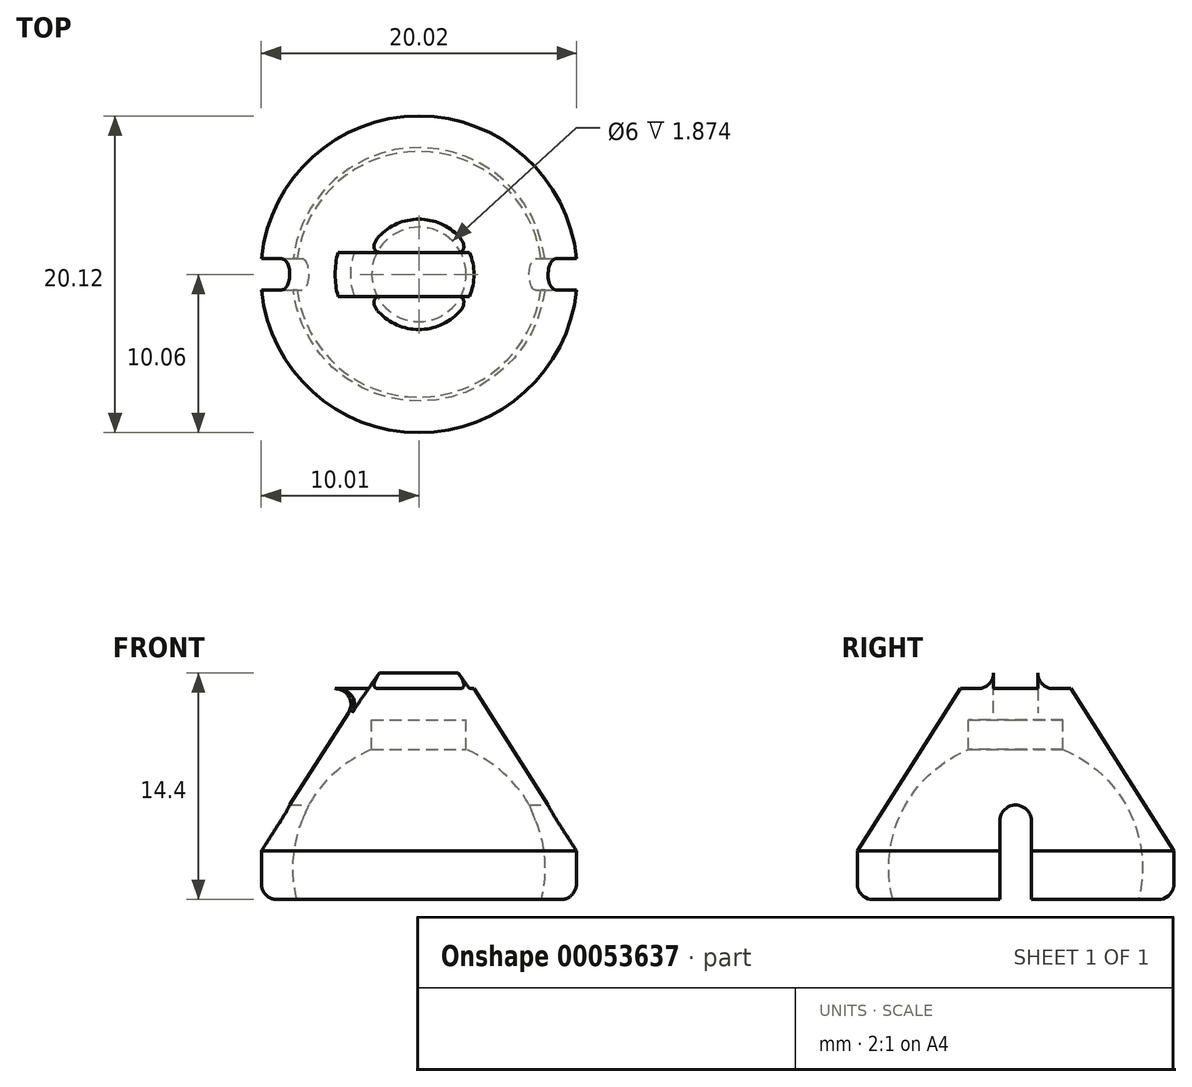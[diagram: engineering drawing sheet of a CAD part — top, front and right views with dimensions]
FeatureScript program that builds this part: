
annotation { "Feature Type Name" : "Feature", "Feature Type Description" : "" }
export const myFeature = defineFeature(function(context is Context, id is Id, definition is map)
    precondition{}
    {
        {
            var Q0;
            Q0=qCreatedBy(makeId("Front.planeOp"),FACE);
            var sketch = newSketch(context, id + "F0", { "sketchPlane" : qUnion([Q0])});
            skArc(sketch, "E0", {"start": v(0, 4.09) * mm, "mid": v(0.48, 4.1) * mm, "end": v(0.97, 4.15) * mm});
            skLineSegment(sketch, "E1", {"start": v(3.5, 7.49) * mm, "end": v(10.06, -2.83) * mm});
            skLineSegment(sketch, "E2", {"start": v(10.06, -2.83) * mm, "end": v(10.06, -5.91) * mm});
            skLineSegment(sketch, "E3", {"start": v(10.06, -5.91) * mm, "end": v(7.8, -5.91) * mm});
            skArc(sketch, "E4", {"start": v(7.8, -5.91) * mm, "mid": v(6.65, 0.66) * mm, "end": v(0.97, 4.15) * mm});
            skPoint(sketch, "E5.orphan", {"position": v(0, -5.91) * mm});
            skLineSegment(sketch, "E6", {"start": v(0, 4.09) * mm, "end": v(0, -5.91) * mm, "construction": true});
            skLineSegment(sketch, "E7", {"start": v(0, 4.09) * mm, "end": v(0, 7.49) * mm});
            skLineSegment(sketch, "E8", {"start": v(0, 7.49) * mm, "end": v(0, 9.49) * mm});
            skLineSegment(sketch, "E9", {"start": v(0, 9.49) * mm, "end": v(3.5, 9.49) * mm});
            skLineSegment(sketch, "E10", {"start": v(3.5, 9.49) * mm, "end": v(3.5, 7.49) * mm});
            skSolve(sketch);
        }
        {
            var Q0;
            Q0=qSketchRegion(id+"F0",true);
            var Q1;
            Q1=sQuery(id+"F0.wireOp",EDGE,"E6");
            revolve(context, id + "F1", {"entities" : qUnion([Q0]), "axis" : qUnion([Q1]), "revolveType" : RevolveType.FULL});
        }
        {
            var Q0;
            Q0=qCreatedBy(makeId("Top.planeOp"),FACE);
            var sketch = newSketch(context, id + "F2", { "sketchPlane" : qUnion([Q0])});
            skCircle(sketch, "E11", {"center": v(0, 0) * mm, "radius": 3 * mm});
            skSolve(sketch);
        }
        {
            var Q0;
            Q0=qSketchRegion(id+"F2",true);
            extrude(context, id + "F3", {"entities" : qUnion([Q0]), "operationType" : NewBodyOperationType.REMOVE, "endBound" : BoundingType.SYMMETRIC, "oppositeDirection" : true, "depth" : 50 * mm});
        }
        {
            var Q0;
            Q0=qCreatedBy(makeId("Right.planeOp"),FACE);
            var sketch = newSketch(context, id + "F4", { "sketchPlane" : qUnion([Q0])});
            skLineSegment(sketch, "E12.bottom", {"start": v(1, -5.91) * mm, "end": v(-1, -5.91) * mm});
            skLineSegment(sketch, "E12.left", {"start": v(1, -5.91) * mm, "end": v(1, -0.91) * mm});
            skLineSegment(sketch, "E12.right", {"start": v(-1, -5.91) * mm, "end": v(-1, -0.91) * mm});
            skArc(sketch, "E13", {"start": v(1, -0.91) * mm, "mid": v(0, 0.09) * mm, "end": v(-1, -0.91) * mm});
            skSolve(sketch);
        }
        {
            var Q0;
            Q0=qSketchRegion(id+"F4",true);
            extrude(context, id + "F5", {"entities" : qUnion([Q0]), "operationType" : NewBodyOperationType.REMOVE, "endBound" : BoundingType.SYMMETRIC, "oppositeDirection" : true, "depth" : 25 * mm});
        }
        {
            var Q0;
            Q0=makeQuery(id+"F1.opRevolve","SWEPT_EDGE",EDGE,{"disambiguationData":[OSD([sQuery(id+"F0.wireOp",EDGE,"E9"),sQuery(id+"F0.wireOp",EDGE,"E10")])]});
            fillet(context, id + "F6", {"entities" : qUnion([Q0]), "radius" : 1 * mm, "tangentPropagation" : true, "allowEdgeOverflow" : false});
        }
        {
            var Q0;
            {var subQ0=sQuery(id+"F0.wireOp",EDGE,"E2");var subQ1=sQuery(id+"F0.wireOp",EDGE,"E3");Q0=makeQuery(id+"F5.boolean.opBoolean","SPLIT",EDGE,{"disambiguationData":[TD([makeQuery(id+"F5.opExtrude","SWEPT_FACE",FACE,{"disambiguationData":[OSD([sQuery(id+"F4.wireOp",EDGE,"E12.right")])]})])],"derivedFrom":makeQuery(id+"F1.opRevolve","SWEPT_EDGE",EDGE,{"disambiguationData":[OSD([subQ0,subQ1])]})});}
            var Q1;
            {var subQ0=sQuery(id+"F0.wireOp",EDGE,"E2");var subQ1=sQuery(id+"F0.wireOp",EDGE,"E3");Q1=makeQuery(id+"F5.boolean.opBoolean","SPLIT",EDGE,{"disambiguationData":[TD([makeQuery(id+"F5.opExtrude","SWEPT_FACE",FACE,{"disambiguationData":[OSD([sQuery(id+"F4.wireOp",EDGE,"E12.left")])]})])],"derivedFrom":makeQuery(id+"F1.opRevolve","SWEPT_EDGE",EDGE,{"disambiguationData":[OSD([subQ0,subQ1])]})});}
            fillet(context, id + "F7", {"entities" : qUnion([Q0, Q1]), "radius" : 1 * mm, "tangentPropagation" : true, "allowEdgeOverflow" : false});
        }
        {
            var Q0;
            Q0=qCreatedBy(makeId("Front.planeOp"),FACE);
            var sketch = newSketch(context, id + "F8", { "sketchPlane" : qUnion([Q0])});
            skLineSegment(sketch, "E14.bottom", {"start": v(-13.5, 17.49) * mm, "end": v(13.5, 17.49) * mm});
            skLineSegment(sketch, "E14.top", {"start": v(-13.5, 7.49) * mm, "end": v(13.5, 7.49) * mm});
            skLineSegment(sketch, "E14.left", {"start": v(-13.5, 17.49) * mm, "end": v(-13.5, 7.49) * mm});
            skLineSegment(sketch, "E14.right", {"start": v(13.5, 17.49) * mm, "end": v(13.5, 7.49) * mm});
            skSolve(sketch);
        }
        {
            var Q0;
            Q0 = qSketchRegion(id + "F8", true);
            extrude(context, id + "F9", {"entities" : qUnion([Q0]), "operationType" : NewBodyOperationType.ADD, "endBound" : BoundingType.SYMMETRIC, "depth" : 7 * mm, "offsetDistance" : 25 * mm});
        }
        {
            var Q0;
            Q0=makeQuery(id+"F9.opExtrude","SWEPT_FACE",FACE,{"disambiguationData":[OSD([sQuery(id+"F8.wireOp",EDGE,"E14.bottom")])]});
            var sketch = newSketch(context, id + "F10", { "sketchPlane" : qUnion([Q0])});
            skLineSegment(sketch, "E15.bottom", {"start": v(-12.75, 2.5) * mm, "end": v(-11.5, 2.5) * mm});
            skLineSegment(sketch, "E15.top", {"start": v(-12.75, 1.4) * mm, "end": v(12.75, 1.4) * mm});
            skLineSegment(sketch, "E15.left", {"start": v(-12.75, 2.5) * mm, "end": v(-12.75, 1.4) * mm});
            skLineSegment(sketch, "E15.right", {"start": v(12.75, 2.5) * mm, "end": v(12.75, 1.4) * mm});
            skLineSegment(sketch, "E16", {"start": v(-11.5, 2.5) * mm, "end": v(-11.5, 3.5) * mm});
            skLineSegment(sketch, "E17", {"start": v(-11.5, 3.5) * mm, "end": v(11.5, 3.5) * mm});
            skLineSegment(sketch, "E18", {"start": v(11.5, 3.5) * mm, "end": v(11.5, 2.5) * mm});
            skLineSegment(sketch, "E19.trimOffspring", {"start": v(11.5, 2.5) * mm, "end": v(12.75, 2.5) * mm});
            skLineSegment(sketch, "E20.MirrorCS", {"start": v(-11.5, -3.5) * mm, "end": v(11.5, -3.5) * mm});
            skLineSegment(sketch, "E21.MirrorCS", {"start": v(-12.75, -1.4) * mm, "end": v(12.75, -1.4) * mm});
            skLineSegment(sketch, "E22.MirrorCS", {"start": v(12.75, -2.5) * mm, "end": v(12.75, -1.4) * mm});
            skLineSegment(sketch, "E23.MirrorCS", {"start": v(11.5, -2.5) * mm, "end": v(12.75, -2.5) * mm});
            skLineSegment(sketch, "E24.MirrorCS", {"start": v(11.5, -3.5) * mm, "end": v(11.5, -2.5) * mm});
            skLineSegment(sketch, "E25.MirrorCS", {"start": v(-11.5, -2.5) * mm, "end": v(-11.5, -3.5) * mm});
            skLineSegment(sketch, "E26.MirrorCS", {"start": v(-12.75, -2.5) * mm, "end": v(-11.5, -2.5) * mm});
            skLineSegment(sketch, "E27.MirrorCS", {"start": v(-12.75, -2.5) * mm, "end": v(-12.75, -1.4) * mm});
            skSolve(sketch);
        }
        {
            var Q0;
            Q0 = qSketchRegion(id + "F10", true);
            var Q1;
            {var subQ0=sQuery(id+"F8.wireOp",EDGE,"E14.right");var subQ2=sQuery(id+"F8.wireOp",EDGE,"E14.top");var subQ4=makeQuery(id+"F9.opExtrude","SWEPT_FACE",FACE,{"disambiguationData":[OSD([subQ2])]});Q1=makeQuery(id+"F9.boolean.opBoolean","SPLIT",FACE,{"disambiguationData":[TD([makeQuery(id+"F9.opExtrude","SWEPT_FACE",FACE,{"disambiguationData":[OSD([subQ0])]})])],"derivedFrom":subQ4});}
            extrude(context, id + "F11", {"entities" : qUnion([Q0]), "operationType" : NewBodyOperationType.REMOVE, "endBound" : BoundingType.UP_TO_SURFACE, "oppositeDirection" : true, "depth" : 25 * mm, "endBoundEntityFace" : qUnion([Q1]), "offsetDistance" : 25 * mm});
        }
        {
            var Q0;
            Q0=makeQuery(id+"F9.boolean.opBoolean","SPLIT",FACE,{"disambiguationData":[TD([makeQuery(id+"F3.boolean.opBoolean","COPY",FACE,{"derivedFrom":makeQuery(id+"F3.opExtrude","SWEPT_FACE",FACE,{"disambiguationData":[OSD([sQuery(id+"F2.wireOp",EDGE,"E11")])]})})])],"derivedFrom":makeQuery(id+"F9.opExtrude","SWEPT_FACE",FACE,{"disambiguationData":[OSD([sQuery(id+"F8.wireOp",EDGE,"E14.top")])]})});
            var sketch = newSketch(context, id + "F12", { "sketchPlane" : qUnion([Q0])});
            skCircle(sketch, "E28", {"center": v(0, 0) * mm, "radius": 3.07 * mm});
            skSolve(sketch);
        }
        {
            var Q0;
            Q0 = qSketchRegion(id + "F12", true);
            extrude(context, id + "F13", {"entities" : qUnion([Q0]), "operationType" : NewBodyOperationType.ADD, "depth" : 2 * mm, "offsetDistance" : 25 * mm});
        }
        {
            var Q0;
            {var subQ0=sQuery(id+"F10.wireOp",EDGE,"E21.MirrorCS");var subQ1=makeQuery(id+"F11.opExtrude","SWEPT_FACE",FACE,{"disambiguationData":[OSD([subQ0])]});var subQ2=makeQuery(id+"F11.opExtrude","CAP_FACE",FACE,{"disambiguationData":[OSD([subQ0,sQuery(id+"F10.wireOp",EDGE,"E22.MirrorCS"),sQuery(id+"F10.wireOp",EDGE,"E23.MirrorCS"),sQuery(id+"F10.wireOp",EDGE,"E24.MirrorCS"),sQuery(id+"F10.wireOp",EDGE,"E25.MirrorCS"),sQuery(id+"F10.wireOp",EDGE,"E26.MirrorCS"),sQuery(id+"F10.wireOp",EDGE,"E27.MirrorCS"),sQuery(id+"F10.wireOp",EDGE,"E20.MirrorCS")])],"isStart":false});var subQ3=makeQuery(id+"F11.opExtrude","CAP_EDGE",EDGE,{"disambiguationData":[OSD([subQ0])],"isStart":false});var subQ4=makeQuery(id+"F9.opExtrude","SWEPT_FACE",FACE,{"disambiguationData":[OSD([sQuery(id+"F8.wireOp",EDGE,"E14.top")])]});Q0=makeQuery(id+"F13.boolean.opBoolean","MERGE",EDGE,{"derivedFrom":[makeQuery(id+"F11.boolean.opBoolean","COPY",EDGE,{"disambiguationData":[topologyDisambiguationEdgeConnected([subQ4,subQ1]),TD([makeQuery(id+"F3.boolean.opBoolean","COPY",FACE,{"derivedFrom":makeQuery(id+"F3.opExtrude","SWEPT_FACE",FACE,{"disambiguationData":[OSD([sQuery(id+"F2.wireOp",EDGE,"E11")])]})})])],"derivedFrom":subQ3}),makeQuery(id+"F11.boolean.opBoolean","COPY",EDGE,{"disambiguationData":[topologyDisambiguationEdgeConnected([subQ1,subQ2]),OD(0.0)],"derivedFrom":subQ3}),makeQuery(id+"F11.boolean.opBoolean","COPY",EDGE,{"disambiguationData":[topologyDisambiguationEdgeConnected([subQ1,subQ2]),OD(1.0)],"derivedFrom":subQ3})]});}
            var Q1;
            {var subQ0=sQuery(id+"F10.wireOp",EDGE,"E15.top");var subQ1=makeQuery(id+"F11.opExtrude","CAP_FACE",FACE,{"disambiguationData":[OSD([sQuery(id+"F10.wireOp",EDGE,"E15.bottom"),subQ0,sQuery(id+"F10.wireOp",EDGE,"E15.left"),sQuery(id+"F10.wireOp",EDGE,"E15.right"),sQuery(id+"F10.wireOp",EDGE,"E16"),sQuery(id+"F10.wireOp",EDGE,"E17"),sQuery(id+"F10.wireOp",EDGE,"E18"),sQuery(id+"F10.wireOp",EDGE,"E19.trimOffspring")])],"isStart":false});var subQ2=makeQuery(id+"F11.opExtrude","SWEPT_FACE",FACE,{"disambiguationData":[OSD([subQ0])]});var subQ3=makeQuery(id+"F11.opExtrude","CAP_EDGE",EDGE,{"disambiguationData":[OSD([subQ0])],"isStart":false});var subQ4=makeQuery(id+"F9.opExtrude","SWEPT_FACE",FACE,{"disambiguationData":[OSD([sQuery(id+"F8.wireOp",EDGE,"E14.top")])]});Q1=makeQuery(id+"F13.boolean.opBoolean","MERGE",EDGE,{"derivedFrom":[makeQuery(id+"F11.boolean.opBoolean","COPY",EDGE,{"disambiguationData":[topologyDisambiguationEdgeConnected([subQ4,subQ2]),TD([makeQuery(id+"F3.boolean.opBoolean","COPY",FACE,{"derivedFrom":makeQuery(id+"F3.opExtrude","SWEPT_FACE",FACE,{"disambiguationData":[OSD([sQuery(id+"F2.wireOp",EDGE,"E11")])]})})])],"derivedFrom":subQ3}),makeQuery(id+"F11.boolean.opBoolean","COPY",EDGE,{"disambiguationData":[topologyDisambiguationEdgeConnected([subQ1,subQ2]),OD(0.0)],"derivedFrom":subQ3}),makeQuery(id+"F11.boolean.opBoolean","COPY",EDGE,{"disambiguationData":[topologyDisambiguationEdgeConnected([subQ1,subQ2]),OD(1.0)],"derivedFrom":subQ3})]});}
            var Q2;
            Q2=makeQuery(id+"F11.boolean.opBoolean","COPY",EDGE,{"derivedFrom":makeQuery(id+"F11.opExtrude","SWEPT_EDGE",EDGE,{"disambiguationData":[OSD([sQuery(id+"F10.wireOp",EDGE,"E23.MirrorCS"),sQuery(id+"F10.wireOp",EDGE,"E24.MirrorCS")])]})});
            var Q3;
            Q3=makeQuery(id+"F11.boolean.opBoolean","COPY",EDGE,{"derivedFrom":makeQuery(id+"F11.opExtrude","SWEPT_EDGE",EDGE,{"disambiguationData":[OSD([sQuery(id+"F10.wireOp",EDGE,"E18"),sQuery(id+"F10.wireOp",EDGE,"E19.trimOffspring")])]})});
            var Q4;
            Q4=makeQuery(id+"F11.boolean.opBoolean","COPY",EDGE,{"derivedFrom":makeQuery(id+"F11.opExtrude","SWEPT_EDGE",EDGE,{"disambiguationData":[OSD([sQuery(id+"F10.wireOp",EDGE,"E15.bottom"),sQuery(id+"F10.wireOp",EDGE,"E16")])]})});
            var Q5;
            Q5=makeQuery(id+"F11.boolean.opBoolean","COPY",EDGE,{"derivedFrom":makeQuery(id+"F11.opExtrude","SWEPT_EDGE",EDGE,{"disambiguationData":[OSD([sQuery(id+"F10.wireOp",EDGE,"E25.MirrorCS"),sQuery(id+"F10.wireOp",EDGE,"E26.MirrorCS")])]})});
            fillet(context, id + "F14", {"entities" : qUnion([Q0, Q1, Q2, Q3, Q4, Q5]), "radius" : 1 * mm, "tangentPropagation" : true, "allowEdgeOverflow" : false});
        }
        {
            var Q0;
            Q0=makeQuery(id+"F11.boolean.opBoolean","SPLIT",EDGE,{"derivedFrom":makeQuery(id+"F9.boolean.opBoolean","SPLIT",EDGE,{"disambiguationData":[OD(0.0)],"derivedFrom":makeQuery(id+"F1.opRevolve","SWEPT_EDGE",EDGE,{"disambiguationData":[OSD([sQuery(id+"F0.wireOp",EDGE,"E1"),sQuery(id+"F0.wireOp",EDGE,"E10")])]})})});
            var Q1;
            Q1=makeQuery(id+"F11.boolean.opBoolean","SPLIT",EDGE,{"derivedFrom":makeQuery(id+"F9.boolean.opBoolean","SPLIT",EDGE,{"disambiguationData":[OD(1.0)],"derivedFrom":makeQuery(id+"F1.opRevolve","SWEPT_EDGE",EDGE,{"disambiguationData":[OSD([sQuery(id+"F0.wireOp",EDGE,"E1"),sQuery(id+"F0.wireOp",EDGE,"E10")])]})})});
            var Q2;
            {var subQ0=sQuery(id+"F10.wireOp",EDGE,"E21.MirrorCS");var subQ2=sQuery(id+"F8.wireOp",EDGE,"E14.left");var subQ3=sQuery(id+"F8.wireOp",EDGE,"E14.top");var subQ5=makeQuery(id+"F9.opExtrude","SWEPT_FACE",FACE,{"disambiguationData":[OSD([subQ3])]});var subQ6=makeQuery(id+"F1.opRevolve","SWEPT_FACE",FACE,{"disambiguationData":[OSD([sQuery(id+"F0.wireOp",EDGE,"E1")])]});Q2=makeQuery(id+"F14.opFillet","TWEAK_EDGE",EDGE,{"derivedFrom":[makeQuery(id+"F11.boolean.opBoolean","TWEAK_VERTEX",VERTEX,{"derivedFrom":[subQ6,makeQuery(id+"F9.boolean.opBoolean","SPLIT",FACE,{"disambiguationData":[TD([makeQuery(id+"F9.opExtrude","SWEPT_FACE",FACE,{"disambiguationData":[OSD([subQ2])]})])],"derivedFrom":subQ5}),makeQuery(id+"F11.opExtrude","SWEPT_FACE",FACE,{"disambiguationData":[OSD([subQ0])]}),makeQuery(id+"F11.opExtrude","CAP_FACE",FACE,{"disambiguationData":[OSD([subQ0,sQuery(id+"F10.wireOp",EDGE,"E22.MirrorCS"),sQuery(id+"F10.wireOp",EDGE,"E23.MirrorCS"),sQuery(id+"F10.wireOp",EDGE,"E24.MirrorCS"),sQuery(id+"F10.wireOp",EDGE,"E25.MirrorCS"),sQuery(id+"F10.wireOp",EDGE,"E26.MirrorCS"),sQuery(id+"F10.wireOp",EDGE,"E27.MirrorCS"),sQuery(id+"F10.wireOp",EDGE,"E20.MirrorCS")])],"isStart":false})]})]});}
            var Q3;
            {var subQ0=sQuery(id+"F10.wireOp",EDGE,"E21.MirrorCS");var subQ1=sQuery(id+"F8.wireOp",EDGE,"E14.right");var subQ3=sQuery(id+"F8.wireOp",EDGE,"E14.top");var subQ5=makeQuery(id+"F9.opExtrude","SWEPT_FACE",FACE,{"disambiguationData":[OSD([subQ3])]});var subQ6=makeQuery(id+"F1.opRevolve","SWEPT_FACE",FACE,{"disambiguationData":[OSD([sQuery(id+"F0.wireOp",EDGE,"E1")])]});Q3=makeQuery(id+"F14.opFillet","TWEAK_EDGE",EDGE,{"derivedFrom":[makeQuery(id+"F11.boolean.opBoolean","TWEAK_VERTEX",VERTEX,{"derivedFrom":[subQ6,makeQuery(id+"F9.boolean.opBoolean","SPLIT",FACE,{"disambiguationData":[TD([makeQuery(id+"F9.opExtrude","SWEPT_FACE",FACE,{"disambiguationData":[OSD([subQ1])]})])],"derivedFrom":subQ5}),makeQuery(id+"F11.opExtrude","SWEPT_FACE",FACE,{"disambiguationData":[OSD([subQ0])]}),makeQuery(id+"F11.opExtrude","CAP_FACE",FACE,{"disambiguationData":[OSD([subQ0,sQuery(id+"F10.wireOp",EDGE,"E22.MirrorCS"),sQuery(id+"F10.wireOp",EDGE,"E23.MirrorCS"),sQuery(id+"F10.wireOp",EDGE,"E24.MirrorCS"),sQuery(id+"F10.wireOp",EDGE,"E25.MirrorCS"),sQuery(id+"F10.wireOp",EDGE,"E26.MirrorCS"),sQuery(id+"F10.wireOp",EDGE,"E27.MirrorCS"),sQuery(id+"F10.wireOp",EDGE,"E20.MirrorCS")])],"isStart":false})]})]});}
            var Q4;
            {var subQ0=sQuery(id+"F10.wireOp",EDGE,"E15.top");var subQ1=sQuery(id+"F8.wireOp",EDGE,"E14.right");var subQ3=sQuery(id+"F8.wireOp",EDGE,"E14.top");var subQ5=makeQuery(id+"F9.opExtrude","SWEPT_FACE",FACE,{"disambiguationData":[OSD([subQ3])]});var subQ6=makeQuery(id+"F1.opRevolve","SWEPT_FACE",FACE,{"disambiguationData":[OSD([sQuery(id+"F0.wireOp",EDGE,"E1")])]});Q4=makeQuery(id+"F14.opFillet","TWEAK_EDGE",EDGE,{"derivedFrom":[makeQuery(id+"F11.boolean.opBoolean","TWEAK_VERTEX",VERTEX,{"derivedFrom":[subQ6,makeQuery(id+"F9.boolean.opBoolean","SPLIT",FACE,{"disambiguationData":[TD([makeQuery(id+"F9.opExtrude","SWEPT_FACE",FACE,{"disambiguationData":[OSD([subQ1])]})])],"derivedFrom":subQ5}),makeQuery(id+"F11.opExtrude","CAP_FACE",FACE,{"disambiguationData":[OSD([sQuery(id+"F10.wireOp",EDGE,"E15.bottom"),subQ0,sQuery(id+"F10.wireOp",EDGE,"E15.left"),sQuery(id+"F10.wireOp",EDGE,"E15.right"),sQuery(id+"F10.wireOp",EDGE,"E16"),sQuery(id+"F10.wireOp",EDGE,"E17"),sQuery(id+"F10.wireOp",EDGE,"E18"),sQuery(id+"F10.wireOp",EDGE,"E19.trimOffspring")])],"isStart":false}),makeQuery(id+"F11.opExtrude","SWEPT_FACE",FACE,{"disambiguationData":[OSD([subQ0])]})]})]});}
            var Q5;
            {var subQ0=sQuery(id+"F10.wireOp",EDGE,"E15.top");var subQ2=sQuery(id+"F8.wireOp",EDGE,"E14.left");var subQ3=sQuery(id+"F8.wireOp",EDGE,"E14.top");var subQ5=makeQuery(id+"F9.opExtrude","SWEPT_FACE",FACE,{"disambiguationData":[OSD([subQ3])]});var subQ6=makeQuery(id+"F1.opRevolve","SWEPT_FACE",FACE,{"disambiguationData":[OSD([sQuery(id+"F0.wireOp",EDGE,"E1")])]});Q5=makeQuery(id+"F14.opFillet","TWEAK_EDGE",EDGE,{"derivedFrom":[makeQuery(id+"F11.boolean.opBoolean","TWEAK_VERTEX",VERTEX,{"derivedFrom":[subQ6,makeQuery(id+"F9.boolean.opBoolean","SPLIT",FACE,{"disambiguationData":[TD([makeQuery(id+"F9.opExtrude","SWEPT_FACE",FACE,{"disambiguationData":[OSD([subQ2])]})])],"derivedFrom":subQ5}),makeQuery(id+"F11.opExtrude","CAP_FACE",FACE,{"disambiguationData":[OSD([sQuery(id+"F10.wireOp",EDGE,"E15.bottom"),subQ0,sQuery(id+"F10.wireOp",EDGE,"E15.left"),sQuery(id+"F10.wireOp",EDGE,"E15.right"),sQuery(id+"F10.wireOp",EDGE,"E16"),sQuery(id+"F10.wireOp",EDGE,"E17"),sQuery(id+"F10.wireOp",EDGE,"E18"),sQuery(id+"F10.wireOp",EDGE,"E19.trimOffspring")])],"isStart":false}),makeQuery(id+"F11.opExtrude","SWEPT_FACE",FACE,{"disambiguationData":[OSD([subQ0])]})]})]});}
            var Q6;
            Q6=makeQuery(id+"F11.boolean.opBoolean","COPY",EDGE,{"derivedFrom":makeQuery(id+"F11.opExtrude","CAP_EDGE",EDGE,{"disambiguationData":[OSD([sQuery(id+"F10.wireOp",EDGE,"E15.top")])],"isStart":true})});
            var Q7;
            Q7=makeQuery(id+"F11.boolean.opBoolean","COPY",EDGE,{"derivedFrom":makeQuery(id+"F11.opExtrude","CAP_EDGE",EDGE,{"disambiguationData":[OSD([sQuery(id+"F10.wireOp",EDGE,"E15.left")])],"isStart":true})});
            var Q8;
            Q8=makeQuery(id+"F11.boolean.opBoolean","COPY",EDGE,{"derivedFrom":makeQuery(id+"F11.opExtrude","CAP_EDGE",EDGE,{"disambiguationData":[OSD([sQuery(id+"F10.wireOp",EDGE,"E15.bottom")])],"isStart":true})});
            var Q9;
            Q9=makeQuery(id+"F11.boolean.opBoolean","COPY",EDGE,{"derivedFrom":makeQuery(id+"F11.opExtrude","CAP_EDGE",EDGE,{"disambiguationData":[OSD([sQuery(id+"F10.wireOp",EDGE,"E21.MirrorCS")])],"isStart":true})});
            var Q10;
            Q10=makeQuery(id+"F11.boolean.opBoolean","COPY",EDGE,{"derivedFrom":makeQuery(id+"F11.opExtrude","CAP_EDGE",EDGE,{"disambiguationData":[OSD([sQuery(id+"F10.wireOp",EDGE,"E27.MirrorCS")])],"isStart":true})});
            var Q11;
            Q11=makeQuery(id+"F11.boolean.opBoolean","COPY",EDGE,{"derivedFrom":makeQuery(id+"F11.opExtrude","CAP_EDGE",EDGE,{"disambiguationData":[OSD([sQuery(id+"F10.wireOp",EDGE,"E26.MirrorCS")])],"isStart":true})});
            var Q12;
            Q12=makeQuery(id+"F11.boolean.opBoolean","COPY",EDGE,{"derivedFrom":makeQuery(id+"F11.opExtrude","CAP_EDGE",EDGE,{"disambiguationData":[OSD([sQuery(id+"F10.wireOp",EDGE,"E22.MirrorCS")])],"isStart":true})});
            var Q13;
            Q13=makeQuery(id+"F11.boolean.opBoolean","COPY",EDGE,{"derivedFrom":makeQuery(id+"F11.opExtrude","CAP_EDGE",EDGE,{"disambiguationData":[OSD([sQuery(id+"F10.wireOp",EDGE,"E23.MirrorCS")])],"isStart":true})});
            var Q14;
            Q14=makeQuery(id+"F11.boolean.opBoolean","COPY",EDGE,{"derivedFrom":makeQuery(id+"F11.opExtrude","CAP_EDGE",EDGE,{"disambiguationData":[OSD([sQuery(id+"F10.wireOp",EDGE,"E15.right")])],"isStart":true})});
            var Q15;
            Q15=makeQuery(id+"F11.boolean.opBoolean","COPY",EDGE,{"derivedFrom":makeQuery(id+"F11.opExtrude","CAP_EDGE",EDGE,{"disambiguationData":[OSD([sQuery(id+"F10.wireOp",EDGE,"E19.trimOffspring")])],"isStart":true})});
            fillet(context, id + "F15", {"entities" : qUnion([Q0, Q1, Q2, Q3, Q4, Q5, Q6, Q7, Q8, Q9, Q10, Q11, Q12, Q13, Q14, Q15]), "radius" : 1 * mm, "tangentPropagation" : true, "allowEdgeOverflow" : false});
        }
        {
            var Q0;
            Q0=makeQuery(id+"F9.opExtrude","SWEPT_FACE",FACE,{"disambiguationData":[OSD([sQuery(id+"F8.wireOp",EDGE,"E14.bottom")])]});
            var sketch = newSketch(context, id + "F16", { "sketchPlane" : qUnion([Q0])});
            skLineSegment(sketch, "E29.bottom", {"start": v(-10.75, 2.5) * mm, "end": v(10.75, 2.5) * mm});
            skLineSegment(sketch, "E29.top", {"start": v(-10.75, -2.81) * mm, "end": v(10.75, -2.81) * mm});
            skLineSegment(sketch, "E29.left", {"start": v(-10.75, 2.5) * mm, "end": v(-10.75, -2.81) * mm});
            skLineSegment(sketch, "E29.right", {"start": v(10.75, 2.5) * mm, "end": v(10.75, -2.81) * mm});
            skSolve(sketch);
        }
        {
            var Q0;
            Q0 = qSketchRegion(id + "F16", true);
            extrude(context, id + "F17", {"entities" : qUnion([Q0]), "operationType" : NewBodyOperationType.REMOVE, "oppositeDirection" : true, "depth" : 8 * mm, "offsetDistance" : 25 * mm});
        }
        {
            var Q0;
            Q0=makeQuery(id+"F17.boolean.opBoolean","COPY",FACE,{"derivedFrom":makeQuery(id+"F17.opExtrude","CAP_FACE",FACE,{"disambiguationData":[OSD([sQuery(id+"F16.wireOp",EDGE,"E29.bottom"),sQuery(id+"F16.wireOp",EDGE,"E29.top"),sQuery(id+"F16.wireOp",EDGE,"E29.left"),sQuery(id+"F16.wireOp",EDGE,"E29.right")])],"isStart":false})});
            var sketch = newSketch(context, id + "F18", { "sketchPlane" : qUnion([Q0])});
            skLineSegment(sketch, "E30.bottom", {"start": v(-10.75, 1.4) * mm, "end": v(10.75, 1.4) * mm});
            skLineSegment(sketch, "E30.top", {"start": v(-10.75, -1.4) * mm, "end": v(10.75, -1.4) * mm});
            skLineSegment(sketch, "E31.bottom", {"start": v(10.75, 4.64) * mm, "end": v(15.58, 4.64) * mm});
            skLineSegment(sketch, "E31.top", {"start": v(10.75, -4.7) * mm, "end": v(15.58, -4.7) * mm});
            skLineSegment(sketch, "E31.left", {"start": v(10.75, 4.64) * mm, "end": v(10.75, 1.4) * mm});
            skLineSegment(sketch, "E31.right", {"start": v(15.58, 4.64) * mm, "end": v(15.58, -4.7) * mm});
            skLineSegment(sketch, "E32.bottom", {"start": v(-10.75, 4.24) * mm, "end": v(-14.33, 4.24) * mm});
            skLineSegment(sketch, "E32.top", {"start": v(-10.75, -4.95) * mm, "end": v(-14.33, -4.95) * mm});
            skLineSegment(sketch, "E32.right", {"start": v(-14.33, 4.24) * mm, "end": v(-14.33, -4.95) * mm});
            skLineSegment(sketch, "E33.trimOffspring", {"start": v(-10.75, -1.4) * mm, "end": v(-10.75, -4.95) * mm});
            skLineSegment(sketch, "E34", {"start": v(-10.75, 1.4) * mm, "end": v(-10.75, 4.24) * mm});
            skLineSegment(sketch, "E35.trimOffspring", {"start": v(10.75, -1.4) * mm, "end": v(10.75, -4.7) * mm});
            skSolve(sketch);
        }
        {
            var Q0;
            Q0 = qSketchRegion(id + "F18", true);
            extrude(context, id + "F19", {"entities" : qUnion([Q0]), "operationType" : NewBodyOperationType.REMOVE, "oppositeDirection" : true, "depth" : 2 * mm, "offsetDistance" : 25 * mm});
        }
        {
            var Q0;
            Q0 = qSketchRegion(id + "F18", true);
            extrude(context, id + "F20", {"entities" : qUnion([Q0]), "operationType" : NewBodyOperationType.REMOVE, "depth" : 25 * mm, "offsetDistance" : 25 * mm});
        }
    });
